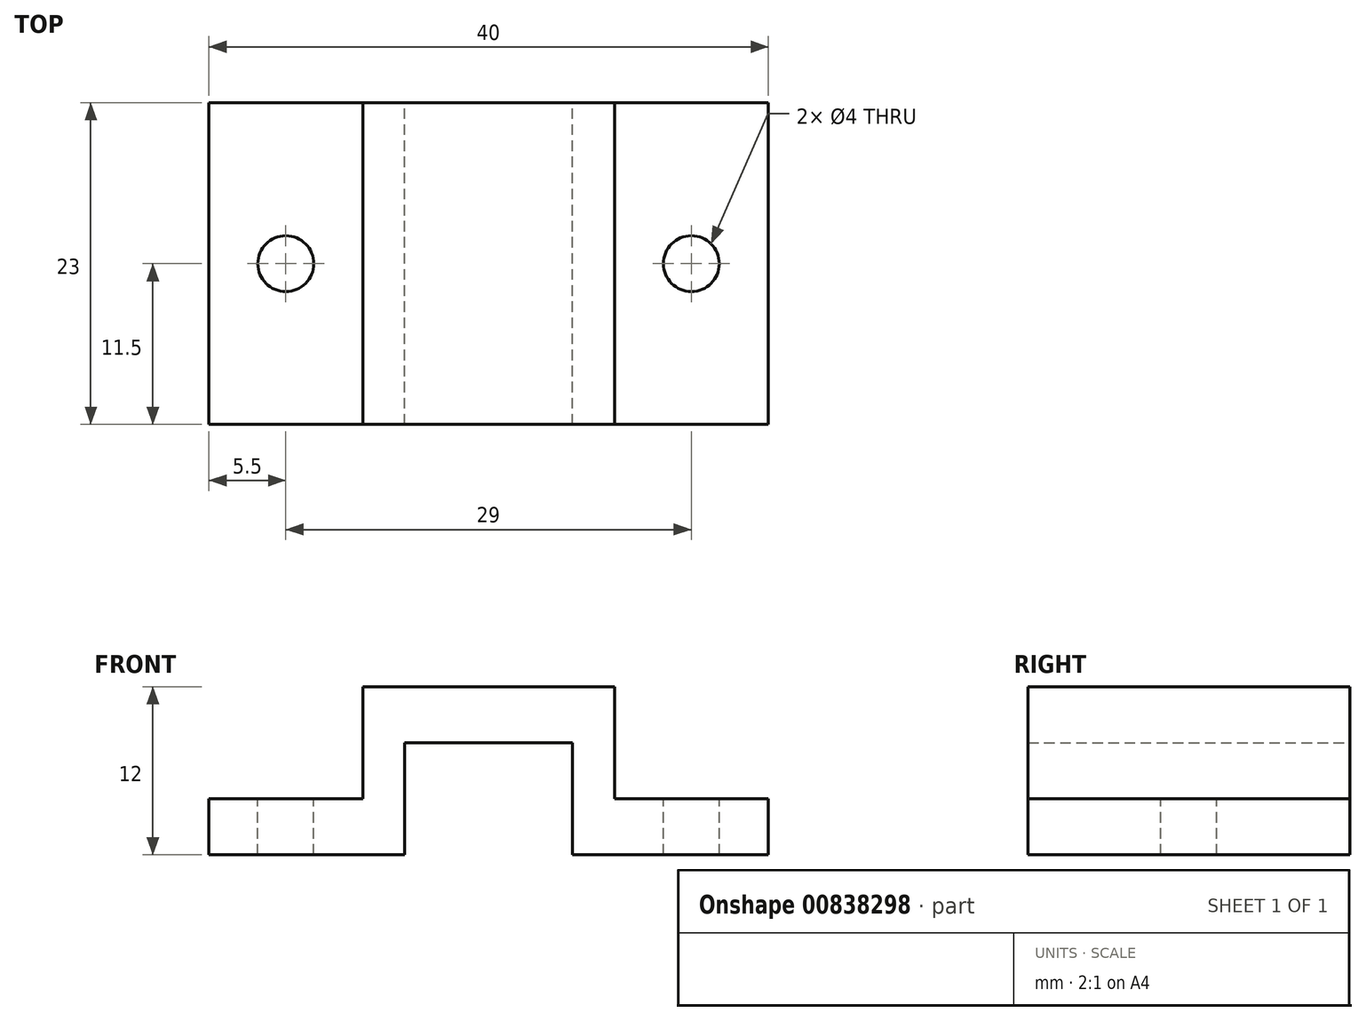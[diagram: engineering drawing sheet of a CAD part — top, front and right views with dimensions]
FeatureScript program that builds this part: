
annotation { "Feature Type Name" : "Feature", "Feature Type Description" : "" }
export const myFeature = defineFeature(function(context is Context, id is Id, definition is map)
    precondition{}
    {
        {
            var Q0;
            Q0=qCreatedBy(makeId("Front.planeOp"),FACE);
            var sketch = newSketch(context, id + "F0", { "sketchPlane" : qUnion([Q0])});
            skLineSegment(sketch, "E0", {"start": v(20, -2) * mm, "end": v(20, -6) * mm});
            skLineSegment(sketch, "E1.MirrorCS", {"start": v(-20, -2) * mm, "end": v(-20, -6) * mm});
            skLineSegment(sketch, "E2.MirrorCS", {"start": v(-20, -6) * mm, "end": v(-6, -6) * mm});
            skLineSegment(sketch, "E3.0", {"start": v(6, 0) * mm, "end": v(6, 2) * mm});
            skLineSegment(sketch, "E4.0", {"start": v(9, -2) * mm, "end": v(20, -2) * mm});
            skPoint(sketch, "E5.start.orphan", {"position": v(0, 0) * mm});
            skLineSegment(sketch, "E6.MirrorCS", {"start": v(8, 6) * mm, "end": v(-8, 6) * mm});
            skLineSegment(sketch, "E7.MirrorCS", {"start": v(6, 2) * mm, "end": v(-6, 2) * mm});
            skLineSegment(sketch, "E8.MirrorCS", {"start": v(-6, 0) * mm, "end": v(-6, 2) * mm});
            skLineSegment(sketch, "E9.MirrorCS", {"start": v(-9, -2) * mm, "end": v(-20, -2) * mm});
            skLineSegment(sketch, "E10.MirrorCS", {"start": v(20, -6) * mm, "end": v(6, -6) * mm});
            skLineSegment(sketch, "E11", {"start": v(-6, 0) * mm, "end": v(-6, -6) * mm});
            skLineSegment(sketch, "E12.MirrorCS", {"start": v(6, 0) * mm, "end": v(6, -6) * mm});
            skLineSegment(sketch, "E13.trimOffspring", {"start": v(-6, -6) * mm, "end": v(-20, -6) * mm});
            skLineSegment(sketch, "E14.trimOffspring", {"start": v(6, -6) * mm, "end": v(20, -6) * mm});
            skLineSegment(sketch, "E15.0", {"start": v(-9, 6) * mm, "end": v(-9, -2) * mm});
            skLineSegment(sketch, "E16", {"start": v(-8, 6) * mm, "end": v(-9, 6) * mm});
            skPoint(sketch, "E17.orphan", {"position": v(-8, -2) * mm});
            skLineSegment(sketch, "E18.MirrorCS", {"start": v(9, 6) * mm, "end": v(9, -2) * mm});
            skLineSegment(sketch, "E19.MirrorCS", {"start": v(8, 6) * mm, "end": v(9, 6) * mm});
            skPoint(sketch, "E20.orphan", {"position": v(8, -2) * mm});
            skSolve(sketch);
        }
        {
            var Q0;
            Q0 = qSketchRegion(id + "F0", true);
            extrude(context, id + "F1", {"entities" : qUnion([Q0]), "depth" : 23 * mm, "offsetDistance" : 25 * mm});
        }
        {
            var Q0;
            Q0=qCreatedBy(makeId("Top.planeOp"),FACE);
            var sketch = newSketch(context, id + "F2", { "sketchPlane" : qUnion([Q0])});
            skCircle(sketch, "E21", {"center": v(-14.5, -11.5) * mm, "radius": 2 * mm});
            skCircle(sketch, "E22.MirrorC", {"center": v(14.5, -11.5) * mm, "radius": 2 * mm});
            skSolve(sketch);
        }
        {
            var Q0;
            Q0 = qSketchRegion(id + "F2", true);
            extrude(context, id + "F3", {"entities" : qUnion([Q0]), "operationType" : NewBodyOperationType.REMOVE, "oppositeDirection" : true, "depth" : 25 * mm, "offsetDistance" : 25 * mm});
        }
    });
